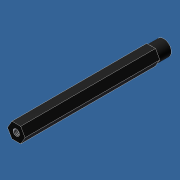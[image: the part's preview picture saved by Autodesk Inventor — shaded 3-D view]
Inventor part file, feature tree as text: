
AUTODESK INVENTOR PART (.ipt)
format: ipt  version: unknown  size: 196,096 bytes
history: native  units: in
note: dims shown in document units (in); Inventor stores cm internally (conversion verified against a paired STEP export)
features: sketch x5, extrude x3, hole x2
ambient origin geometry x8: Origin, YZ Plane, XZ Plane, XY Plane, X Axis, Y Axis, Z Axis, Center Point
bodies: Solid1 (feature_tree)
feature tree (10):
  extrude  "Extrusion1"  Depth=3.625in TaperAngle=0.0deg
  extrude  "Extrusion3"  Depth=0.1in TaperAngle=0.0deg
  extrude  "Extrusion2"  Depth=0.3111in TaperAngle=0.0deg
  hole  "Hole1"  [1 undecoded]
  hole  "Hole2"  [1 undecoded]
  sketch  "Sketch1"  dims[d0=0.375in d1=3.625in d2=0.0in]
  sketch  "Sketch2"  dims[d3=0.1in d4=0.1in d5=0.0in]
  sketch  "Sketch3"  dims[d6=0.375in d7=0.3111in d8=0.0in]
  sketch  "Sketch4"  dims[d9=0.156in d10=0.75in d11=0.375in d12=0.25in d13=0.5635in d14=1.0in d15=0.8108in]
  sketch  "Sketch5"  dims[d16=0.156in d17=0.75in d18=0.375in d19=0.25in d20=0.5635in d21=1.0in d22=0.8108in]
note: 2 required parameter values undecoded (feature->parameter linkage not recoverable at this tier; creation-order binding heuristic only, values carry confidence <= 0.55)
